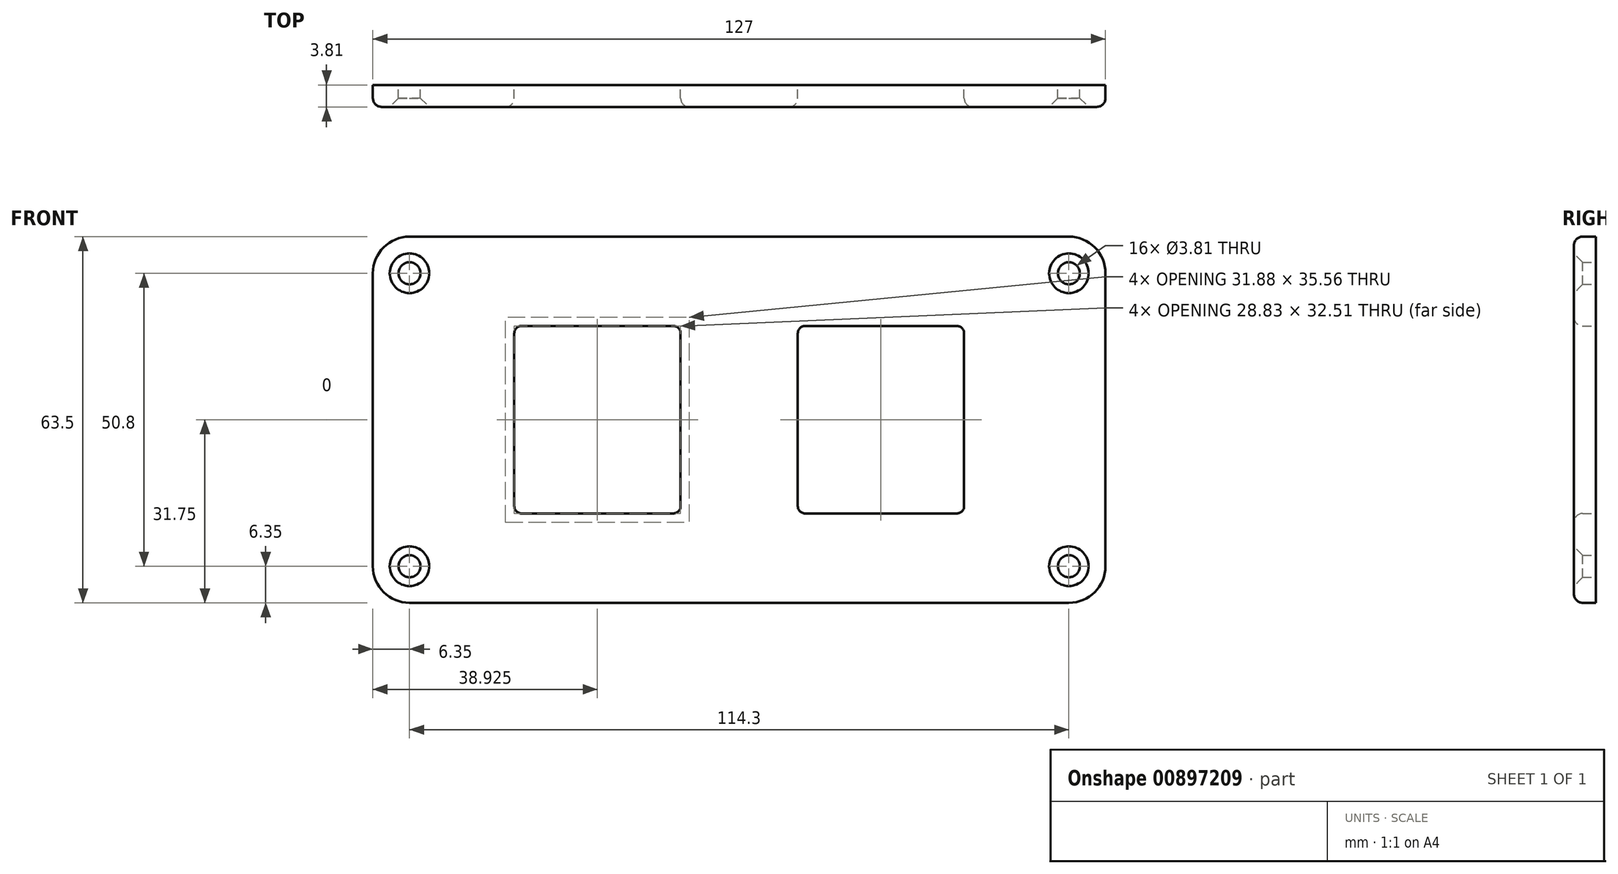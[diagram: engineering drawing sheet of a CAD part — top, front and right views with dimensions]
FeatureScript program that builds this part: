
annotation { "Feature Type Name" : "Feature", "Feature Type Description" : "" }
export const myFeature = defineFeature(function(context is Context, id is Id, definition is map)
    precondition{}
    {
        {
            var Q0;
            Q0=qCreatedBy(makeId("Front.planeOp"),FACE);
            var sketch = newSketch(context, id + "F0", { "sketchPlane" : qUnion([Q0])});
            skLineSegment(sketch, "E0.bottom", {"start": v(57.15, 31.75) * mm, "end": v(-57.15, 31.75) * mm});
            skLineSegment(sketch, "E0.top", {"start": v(57.15, -31.75) * mm, "end": v(-57.15, -31.75) * mm});
            skLineSegment(sketch, "E0.left", {"start": v(63.5, 25.4) * mm, "end": v(63.5, -25.4) * mm});
            skLineSegment(sketch, "E0.right", {"start": v(-63.5, 25.4) * mm, "end": v(-63.5, -25.4) * mm});
            skPoint(sketch, "E0.middle", {"position": v(0, 0) * mm});
            skPoint(sketch, "E1.visualSharp", {"position": v(-63.5, 31.75) * mm});
            skArc(sketch, "E1.filletArc", {"start": v(-57.15, 31.75) * mm, "mid": v(-61.64, 29.9) * mm, "end": v(-63.5, 25.4) * mm});
            skPoint(sketch, "E2.visualSharp", {"position": v(-63.5, -31.75) * mm});
            skArc(sketch, "E2.filletArc", {"start": v(-63.5, -25.4) * mm, "mid": v(-61.64, -29.9) * mm, "end": v(-57.15, -31.75) * mm});
            skPoint(sketch, "E3.visualSharp", {"position": v(63.5, -31.75) * mm});
            skArc(sketch, "E3.filletArc", {"start": v(57.15, -31.75) * mm, "mid": v(61.64, -29.9) * mm, "end": v(63.5, -25.4) * mm});
            skPoint(sketch, "E4.visualSharp", {"position": v(63.5, 31.75) * mm});
            skArc(sketch, "E4.filletArc", {"start": v(63.5, 25.4) * mm, "mid": v(61.64, 29.9) * mm, "end": v(57.15, 31.75) * mm});
            skCircle(sketch, "E5", {"center": v(-57.15, 25.4) * mm, "radius": 1.9 * mm});
            skCircle(sketch, "E6", {"center": v(-57.15, -25.4) * mm, "radius": 1.9 * mm});
            skCircle(sketch, "E7", {"center": v(57.15, -25.4) * mm, "radius": 1.9 * mm});
            skCircle(sketch, "E8", {"center": v(57.15, 25.4) * mm, "radius": 1.9 * mm});
            skLineSegment(sketch, "E9.bottom", {"start": v(-37.72, 16.26) * mm, "end": v(-11.43, 16.26) * mm});
            skLineSegment(sketch, "E9.top", {"start": v(-37.72, -16.26) * mm, "end": v(-11.43, -16.26) * mm});
            skLineSegment(sketch, "E9.left", {"start": v(-38.99, 14.99) * mm, "end": v(-38.99, -14.99) * mm});
            skLineSegment(sketch, "E9.right", {"start": v(-10.16, 14.99) * mm, "end": v(-10.16, -14.99) * mm});
            skLineSegment(sketch, "E10.bottom", {"start": v(11.43, 16.26) * mm, "end": v(37.72, 16.26) * mm});
            skLineSegment(sketch, "E10.top", {"start": v(11.43, -16.26) * mm, "end": v(37.72, -16.26) * mm});
            skLineSegment(sketch, "E10.left", {"start": v(10.16, 14.99) * mm, "end": v(10.16, -14.99) * mm});
            skLineSegment(sketch, "E10.right", {"start": v(38.99, 14.99) * mm, "end": v(38.99, -14.99) * mm});
            skPoint(sketch, "E11.visualSharp", {"position": v(-38.99, 16.26) * mm});
            skArc(sketch, "E11.filletArc", {"start": v(-37.72, 16.26) * mm, "mid": v(-38.62, 15.88) * mm, "end": v(-38.99, 14.99) * mm});
            skPoint(sketch, "E12.visualSharp", {"position": v(-10.16, 16.26) * mm});
            skArc(sketch, "E12.filletArc", {"start": v(-10.16, 14.99) * mm, "mid": v(-10.53, 15.88) * mm, "end": v(-11.43, 16.26) * mm});
            skPoint(sketch, "E13.visualSharp", {"position": v(-10.16, -16.26) * mm});
            skArc(sketch, "E13.filletArc", {"start": v(-11.43, -16.26) * mm, "mid": v(-10.53, -15.88) * mm, "end": v(-10.16, -14.99) * mm});
            skPoint(sketch, "E14.visualSharp", {"position": v(-38.99, -16.26) * mm});
            skArc(sketch, "E14.filletArc", {"start": v(-38.99, -14.99) * mm, "mid": v(-38.62, -15.88) * mm, "end": v(-37.72, -16.26) * mm});
            skPoint(sketch, "E15.visualSharp", {"position": v(10.16, -16.26) * mm});
            skArc(sketch, "E15.filletArc", {"start": v(10.16, -14.99) * mm, "mid": v(10.53, -15.88) * mm, "end": v(11.43, -16.26) * mm});
            skPoint(sketch, "E16.visualSharp", {"position": v(38.99, -16.26) * mm});
            skArc(sketch, "E16.filletArc", {"start": v(37.72, -16.26) * mm, "mid": v(38.62, -15.88) * mm, "end": v(38.99, -14.99) * mm});
            skPoint(sketch, "E17.visualSharp", {"position": v(38.99, 16.26) * mm});
            skArc(sketch, "E17.filletArc", {"start": v(38.99, 14.99) * mm, "mid": v(38.62, 15.88) * mm, "end": v(37.72, 16.26) * mm});
            skPoint(sketch, "E18.visualSharp", {"position": v(10.16, 16.26) * mm});
            skArc(sketch, "E18.filletArc", {"start": v(11.43, 16.26) * mm, "mid": v(10.53, 15.88) * mm, "end": v(10.16, 14.99) * mm});
            skSolve(sketch);
        }
        {
            var Q0;
            Q0=makeQuery(id+"F0.imprint","IMPRINT",FACE,{"disambiguationData":[TD([[makeQuery(id+"F0.imprint","IMPRINT",EDGE,{"derivedFrom":sQuery(id+"F0.wireOp",EDGE,"E0.bottom")}),1.0]])]});
            extrude(context, id + "F1", {"entities" : qUnion([Q0]), "depth" : 3.8 * mm, "offsetDistance" : 25.4 * mm});
        }
        {
            var Q0;
            Q0=makeQuery(id+"F1.opExtrude","CAP_EDGE",EDGE,{"disambiguationData":[OSD([sQuery(id+"F0.wireOp",EDGE,"E9.left")])],"isStart":false});
            var Q1;
            Q1=makeQuery(id+"F1.opExtrude","CAP_EDGE",EDGE,{"disambiguationData":[OSD([sQuery(id+"F0.wireOp",EDGE,"E10.left")])],"isStart":false});
            var Q2;
            Q2=makeQuery(id+"F1.opExtrude","CAP_EDGE",EDGE,{"disambiguationData":[OSD([sQuery(id+"F0.wireOp",EDGE,"E0.right")])],"isStart":false});
            fillet(context, id + "F2", {"entities" : qUnion([Q0, Q1, Q2]), "radius" : 1.52 * mm, "tangentPropagation" : true, "allowEdgeOverflow" : false});
        }
        {
            var Q0;
            Q0=makeQuery(id+"F1.opExtrude","CAP_EDGE",EDGE,{"disambiguationData":[OSD([sQuery(id+"F0.wireOp",EDGE,"E5")])],"isStart":false});
            var Q1;
            Q1=makeQuery(id+"F1.opExtrude","CAP_EDGE",EDGE,{"disambiguationData":[OSD([sQuery(id+"F0.wireOp",EDGE,"E6")])],"isStart":false});
            var Q2;
            Q2=makeQuery(id+"F1.opExtrude","CAP_EDGE",EDGE,{"disambiguationData":[OSD([sQuery(id+"F0.wireOp",EDGE,"E7")])],"isStart":false});
            var Q3;
            Q3=makeQuery(id+"F1.opExtrude","CAP_EDGE",EDGE,{"disambiguationData":[OSD([sQuery(id+"F0.wireOp",EDGE,"E8")])],"isStart":false});
            chamfer(context, id + "F3", {"entities" : qUnion([Q0, Q1, Q2, Q3]), "width" : 1.52 * mm, "tangentPropagation" : true});
        }
    });
